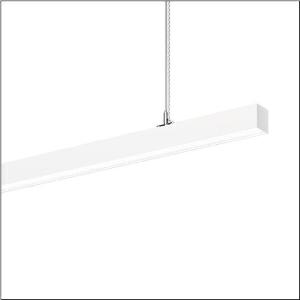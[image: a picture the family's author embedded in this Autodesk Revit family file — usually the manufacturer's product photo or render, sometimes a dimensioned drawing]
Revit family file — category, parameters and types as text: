
# Revit family: silica_r__21_51mx33db39wb_e509
name_source: partatom
category: Lighting Fixtures
units: mm (PartAtom-declared; Revit-internal decimal feet)

## family parameters
Cut with Voids When Loaded = No
Host = Face
Light Source = No
Part Type = Normal
Room Calculation Point = No
Round Connector Dimension = Use Diameter
Shared = No

## types (1)
- --- (1 x LED, 7390 lm, 51.6 W, 3000K)
    Apparent Load = 52 VA
    CIE Flux Codes = 78 96 99 55 100
    Color Rendering = 80
    Color Temperature = 3000K
    Default Elevation = 1800 mm
    Description = Silica® 21, office luminaire, primary optical cover: prismatic diffuser, of PMMA, CAT 2 (L<= 3000cd/m²), light emission: direct/indirect distribution, primary light characteristic: symmetric, installation type: suspended mounting, LED, rated luminous flux: 7.390lm, luminous efficacy: 143lm/W, light colour: 830, colour temperature: 3000K, with terminal, 3+2-pole, max. 2.5mm², mains connection: 220..240V, AC, 50/60Hz, rated input power: 51.6W, luminaire housing, of aluminium, traffic white (RAL 9016), length: 1.504mm, width: 53mm, height: 53mm, protection rating (complete): IP20, insulation class (complete): insulation class I (protective earthing), certification: CE, permissible operating ambient temperature: 0..+35°C, standard: EN 50419, packaging unit: 1 piece
    Height = 53 mm
    Lamp = 1 x LED
    Lamp Light Flux = 7390 lm
    Lamp Power = 51.6 W
    Lamp count = 1
    Length = 1504 mm
    Luminous efficacy = 143 lm/W
    Manufacturer = Siteco
    ModVariant = No
    Model = 51MX33DB39WB
    Mounting Place = Ceiling
    Mounting Type = Pendant
    Number of Poles = 1
    OnlyDefault = Yes
    Power Factor = 1
    Product Name = Silica® 21
    Product group = office luminaire | ceiling pendant
    ProductGroupID = 902
    Protection Class = Protection class I
    Protection Degree = IP 20
    RLX_Detail_Level = 1
    RLX_Emergency_Light_Flux = 0 lm
    RLX_Emergency_Type = 0
    RLX_Emergency_Type_DB = No
    RlxData = <blob elided: 21361 chars, md5=e3b74553>
    Socket = socket
    Standby Power = 0 W
    System Light Flux = 7390 lm
    System Power = 52 W
    Type Comments = factory setting: luminous flux: 100 % | dim-lin: 254 | 345 mA
    Type Image = l_1297784.jpg
    URL = http://relux.com
    VarID = @adj_048611
    Voltage = 0 V
    Weight = 0.00 kg
    Width = 53 mm

## geometry (parser evidence)
native form markers: Blend x4, Sweep x14
no freeform markers — native parametric forms only
